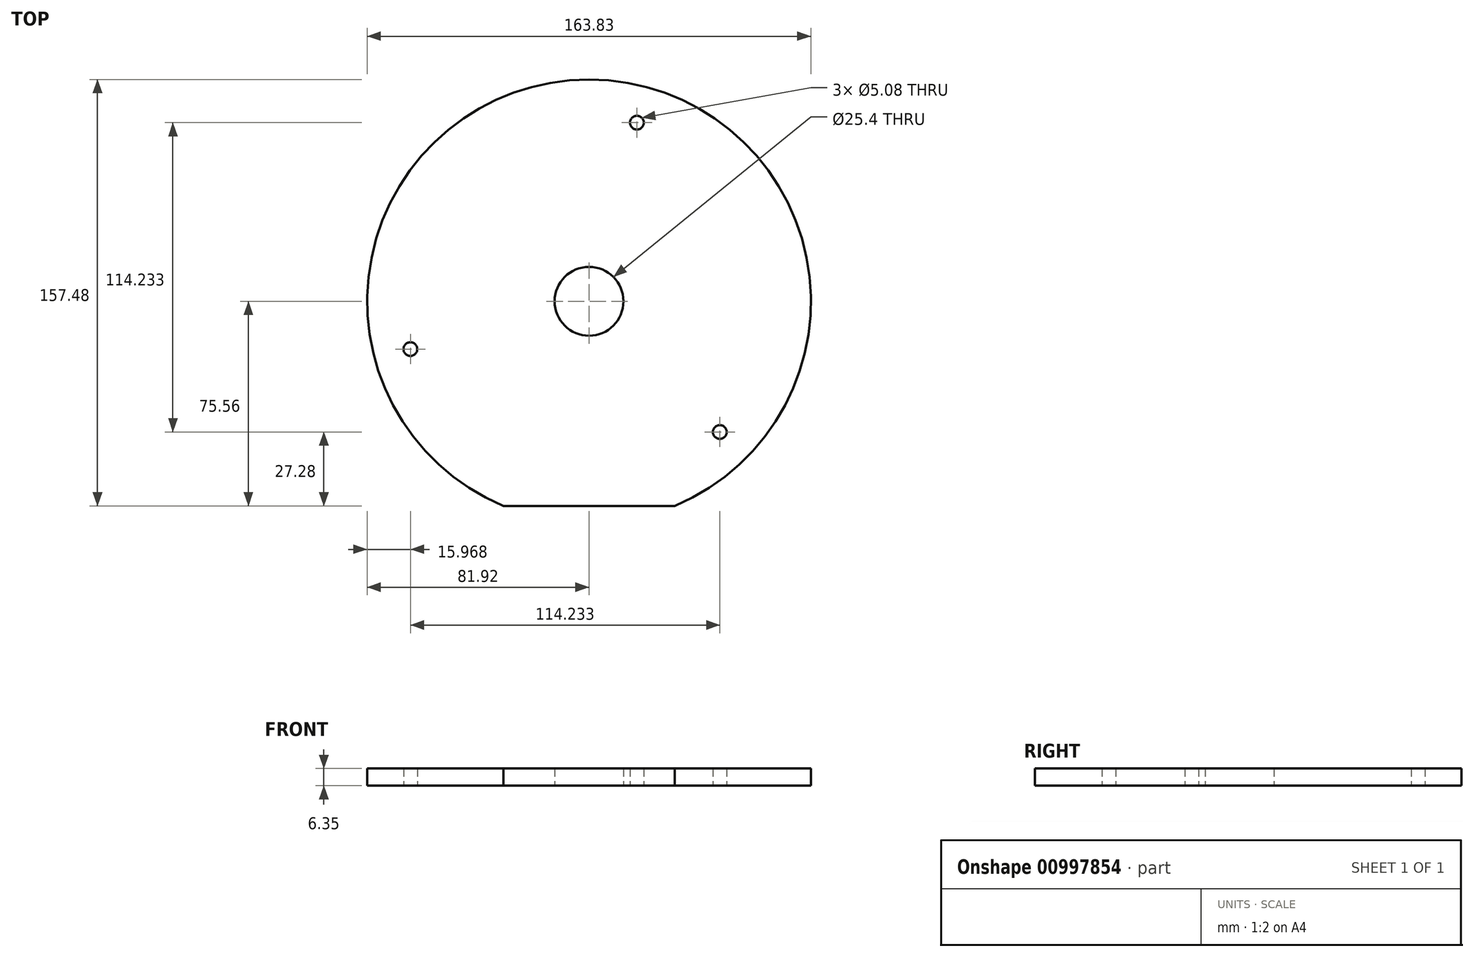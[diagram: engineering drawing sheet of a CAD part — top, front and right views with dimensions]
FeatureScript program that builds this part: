
annotation { "Feature Type Name" : "Feature", "Feature Type Description" : "" }
export const myFeature = defineFeature(function(context is Context, id is Id, definition is map)
    precondition{}
    {
        {
            var Q0;
            Q0=qCreatedBy(makeId("Top.planeOp"),FACE);
            var sketch = newSketch(context, id + "F0", { "sketchPlane" : qUnion([Q0])});
            skCircle(sketch, "E0", {"center": v(0, 0) * mm, "radius": 12.7 * mm});
            skLineSegment(sketch, "E1", {"start": v(-31.62, -75.56) * mm, "end": v(31.62, -75.56) * mm});
            skArc(sketch, "E2", {"start": v(-31.62, -75.57) * mm, "mid": v(0, 81.92) * mm, "end": v(31.62, -75.57) * mm});
            skCircle(sketch, "E3.cCircle", {"center": v(0, 0) * mm, "radius": 68.28 * mm, "construction": true});
            skLineSegment(sketch, "E3.0", {"start": v(48.28, -48.28) * mm, "end": v(-65.95, -17.67) * mm});
            skLineSegment(sketch, "E3.1", {"start": v(-65.95, -17.67) * mm, "end": v(17.67, 65.95) * mm});
            skLineSegment(sketch, "E3.2", {"start": v(17.67, 65.95) * mm, "end": v(48.28, -48.28) * mm});
            skCircle(sketch, "E4", {"center": v(48.28, -48.28) * mm, "radius": 2.54 * mm});
            skCircle(sketch, "E5", {"center": v(17.67, 65.95) * mm, "radius": 2.54 * mm});
            skCircle(sketch, "E6", {"center": v(-65.95, -17.67) * mm, "radius": 2.54 * mm});
            skSolve(sketch);
        }
        {
            var Q0;
            Q0 = qSketchRegion(id + "F0", true);
            var Q1;
            Q1=makeQuery(id+"F0.imprint","IMPRINT",FACE,{"disambiguationData":[TD([[makeQuery(id+"F0.imprint","IMPRINT",EDGE,{"derivedFrom":sQuery(id+"F0.wireOp",EDGE,"E0")}),-1.0]])]});
            extrude(context, id + "F1", {"entities" : qUnion([Q0, Q1]), "depth" : 6.35 * mm, "offsetDistance" : 25.4 * mm});
        }
    });
